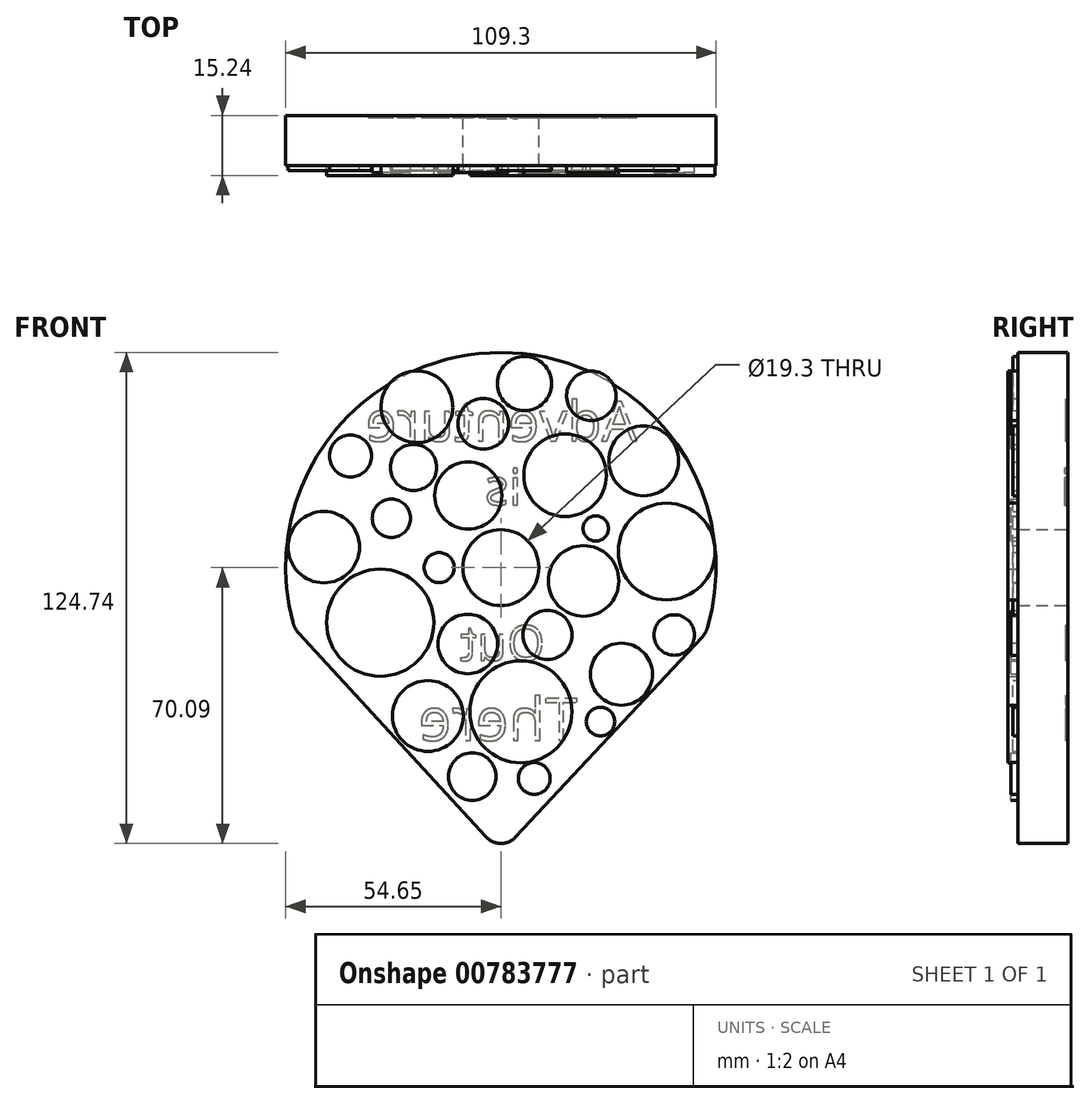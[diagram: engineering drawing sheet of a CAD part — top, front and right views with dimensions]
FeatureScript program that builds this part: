
annotation { "Feature Type Name" : "Feature", "Feature Type Description" : "" }
export const myFeature = defineFeature(function(context is Context, id is Id, definition is map)
    precondition{}
    {
        {
            var Q0;
            Q0=qCreatedBy(makeId("Front.planeOp"),FACE);
            var sketch = newSketch(context, id + "F0", { "sketchPlane" : qUnion([Q0])});
            skCircle(sketch, "E0", {"center": v(0, 0) * mm, "radius": 9.65 * mm});
            skArc(sketch, "E1", {"start": v(52.5, -15.18) * mm, "mid": v(0.62, 54.64) * mm, "end": v(-52.83, -13.99) * mm});
            skLineSegment(sketch, "E2", {"start": v(-51.36, -16.66) * mm, "end": v(-0.8, -71.62) * mm});
            skLineSegment(sketch, "E3", {"start": v(0.07, -72.4) * mm, "end": v(51.04, -17.75) * mm});
            skPoint(sketch, "E4.visualSharp", {"position": v(0, -72.49) * mm});
            skArc(sketch, "E4.filletArc", {"start": v(-0.8, -71.62) * mm, "mid": v(-0.38, -72.03) * mm, "end": v(0.07, -72.4) * mm});
            skPoint(sketch, "E5.visualSharp", {"position": v(-52.39, -15.54) * mm});
            skArc(sketch, "E5.filletArc", {"start": v(-52.83, -13.99) * mm, "mid": v(-52.26, -15.41) * mm, "end": v(-51.36, -16.66) * mm});
            skPoint(sketch, "E6.visualSharp", {"position": v(52.04, -16.68) * mm});
            skArc(sketch, "E6.filletArc", {"start": v(51.04, -17.75) * mm, "mid": v(51.92, -16.55) * mm, "end": v(52.5, -15.18) * mm});
            skSolve(sketch);
        }
        {
            var Q0;
            Q0=makeQuery(id+"F0.imprint","IMPRINT",FACE,{"disambiguationData":[TD([[makeQuery(id+"F0.imprint","IMPRINT",EDGE,{"derivedFrom":sQuery(id+"F0.wireOp",EDGE,"E0")}),-1.0]])]});
            extrude(context, id + "F1", {"entities" : qUnion([Q0]), "depth" : 12.7 * mm, "offsetDistance" : 25.4 * mm});
        }
        {
            var Q0;
            Q0=makeQuery(id+"F1.opExtrude","CAP_FACE",FACE,{"disambiguationData":[OSD([sQuery(id+"F0.wireOp",EDGE,"E0"),sQuery(id+"F0.wireOp",EDGE,"E1"),sQuery(id+"F0.wireOp",EDGE,"E2"),sQuery(id+"F0.wireOp",EDGE,"E3"),sQuery(id+"F0.wireOp",EDGE,"E4.filletArc"),sQuery(id+"F0.wireOp",EDGE,"E5.filletArc"),sQuery(id+"F0.wireOp",EDGE,"E6.filletArc")])],"isStart":true});
            var sketch = newSketch(context, id + "F2", { "sketchPlane" : qUnion([Q0])});
            skText(sketch, "E7", { "text": "Adventure", "fontName": "NotoSans-Regular.ttf"});
            const initialGuessF2  = {"E7": [-0.03457, 0.03213, 1, 0, 0.01013]};
            skSetInitialGuess(sketch, initialGuessF2);
            skSolve(sketch);
        }
        {
            var Q0;
            Q0 = qSketchRegion(id + "F2", true);
            extrude(context, id + "F3", {"entities" : qUnion([Q0]), "operationType" : NewBodyOperationType.REMOVE, "oppositeDirection" : true, "depth" : 0.5 * mm, "offsetDistance" : 25.4 * mm});
        }
        {
            var Q0;
            {var subQ0=sQuery(id+"F0.wireOp",EDGE,"E1");var subQ1=sQuery(id+"F0.wireOp",EDGE,"E3");var subQ2=sQuery(id+"F0.wireOp",EDGE,"E0");var subQ3=sQuery(id+"F0.wireOp",EDGE,"E4.filletArc");var subQ4=sQuery(id+"F0.wireOp",EDGE,"E5.filletArc");var subQ5=sQuery(id+"F0.wireOp",EDGE,"E6.filletArc");var subQ6=sQuery(id+"F0.wireOp",EDGE,"E2");Q0=makeQuery(id+"F3.boolean.opBoolean","SPLIT",FACE,{"disambiguationData":[TD([makeQuery(id+"F1.opExtrude","SWEPT_FACE",FACE,{"disambiguationData":[OSD([subQ2])]})])],"derivedFrom":makeQuery(id+"F1.opExtrude","CAP_FACE",FACE,{"disambiguationData":[OSD([subQ2,subQ0,subQ6,subQ1,subQ3,subQ4,subQ5])],"isStart":true})});}
            var sketch = newSketch(context, id + "F4", { "sketchPlane" : qUnion([Q0])});
            skText(sketch, "E8", { "text": "is", "fontName": "OpenSans-Regular.ttf"});
            const initialGuessF4  = {"E8": [-0.00527, 0.01596, 1, 0, 0.00921]};
            skSetInitialGuess(sketch, initialGuessF4);
            skSolve(sketch);
        }
        {
            var Q0;
            Q0 = qSketchRegion(id + "F4", true);
            extrude(context, id + "F5", {"entities" : qUnion([Q0]), "operationType" : NewBodyOperationType.REMOVE, "oppositeDirection" : true, "depth" : 0.76 * mm, "offsetDistance" : 25.4 * mm});
        }
        {
            var Q0;
            {var subQ0=sQuery(id+"F0.wireOp",EDGE,"E1");var subQ1=sQuery(id+"F0.wireOp",EDGE,"E3");var subQ2=sQuery(id+"F0.wireOp",EDGE,"E0");var subQ3=sQuery(id+"F0.wireOp",EDGE,"E4.filletArc");var subQ4=sQuery(id+"F0.wireOp",EDGE,"E5.filletArc");var subQ5=sQuery(id+"F0.wireOp",EDGE,"E6.filletArc");var subQ6=sQuery(id+"F0.wireOp",EDGE,"E2");Q0=makeQuery(id+"F3.boolean.opBoolean","SPLIT",FACE,{"disambiguationData":[TD([makeQuery(id+"F1.opExtrude","SWEPT_FACE",FACE,{"disambiguationData":[OSD([subQ2])]})])],"derivedFrom":makeQuery(id+"F1.opExtrude","CAP_FACE",FACE,{"disambiguationData":[OSD([subQ2,subQ0,subQ6,subQ1,subQ3,subQ4,subQ5])],"isStart":true})});}
            var sketch = newSketch(context, id + "F6", { "sketchPlane" : qUnion([Q0])});
            skText(sketch, "E9", { "text": "Out", "fontName": "OpenSans-Regular.ttf"});
            const initialGuessF6  = {"E9": [-0.0112, -0.0236, 1, 0, 0.00894]};
            skSetInitialGuess(sketch, initialGuessF6);
            skSolve(sketch);
        }
        {
            var Q0;
            Q0 = qSketchRegion(id + "F6", true);
            extrude(context, id + "F7", {"entities" : qUnion([Q0]), "operationType" : NewBodyOperationType.REMOVE, "oppositeDirection" : true, "depth" : 0.5 * mm, "offsetDistance" : 25.4 * mm});
        }
        {
            var Q0;
            {var subQ61=sQuery(id+"F0.wireOp",EDGE,"E6.filletArc");var subQ68=sQuery(id+"F0.wireOp",EDGE,"E5.filletArc");var subQ77=sQuery(id+"F0.wireOp",EDGE,"E0");var subQ78=makeQuery(id+"F1.opExtrude","SWEPT_FACE",FACE,{"disambiguationData":[OSD([subQ77])]});var subQ81=sQuery(id+"F0.wireOp",EDGE,"E4.filletArc");var subQ87=sQuery(id+"F0.wireOp",EDGE,"E3");var subQ91=sQuery(id+"F0.wireOp",EDGE,"E1");var subQ94=sQuery(id+"F0.wireOp",EDGE,"E2");Q0=makeQuery(id+"F7.boolean.opBoolean","SPLIT",FACE,{"disambiguationData":[TD([subQ78])],"derivedFrom":makeQuery(id+"F3.boolean.opBoolean","SPLIT",FACE,{"disambiguationData":[TD([subQ78])],"derivedFrom":makeQuery(id+"F1.opExtrude","CAP_FACE",FACE,{"disambiguationData":[OSD([subQ77,subQ91,subQ94,subQ87,subQ81,subQ68,subQ61])],"isStart":true})})});}
            var sketch = newSketch(context, id + "F8", { "sketchPlane" : qUnion([Q0])});
            skText(sketch, "E10", { "text": "There", "fontName": "OpenSans-Regular.ttf"});
            const initialGuessF8  = {"E10": [-0.01947, -0.0439, 1, 0, 0.01079]};
            skSetInitialGuess(sketch, initialGuessF8);
            skSolve(sketch);
        }
        {
            var Q0;
            Q0 = qSketchRegion(id + "F8", true);
            extrude(context, id + "F9", {"entities" : qUnion([Q0]), "operationType" : NewBodyOperationType.REMOVE, "oppositeDirection" : true, "depth" : 0.5 * mm, "offsetDistance" : 25.4 * mm});
        }
        {
            var Q0;
            Q0=makeQuery(id+"F1.opExtrude","CAP_FACE",FACE,{"disambiguationData":[OSD([sQuery(id+"F0.wireOp",EDGE,"E0"),sQuery(id+"F0.wireOp",EDGE,"E1"),sQuery(id+"F0.wireOp",EDGE,"E2"),sQuery(id+"F0.wireOp",EDGE,"E3"),sQuery(id+"F0.wireOp",EDGE,"E4.filletArc"),sQuery(id+"F0.wireOp",EDGE,"E5.filletArc"),sQuery(id+"F0.wireOp",EDGE,"E6.filletArc")])],"isStart":false});
            var sketch = newSketch(context, id + "F10", { "sketchPlane" : qUnion([Q0])});
            skCircle(sketch, "E11", {"center": v(-21.32, 40.87) * mm, "radius": 9.11 * mm});
            skCircle(sketch, "E12", {"center": v(16.3, 23.46) * mm, "radius": 10.48 * mm});
            skCircle(sketch, "E13", {"center": v(-30.64, -13.99) * mm, "radius": 13.62 * mm});
            skCircle(sketch, "E14", {"center": v(30.63, -27.08) * mm, "radius": 7.88 * mm});
            skCircle(sketch, "E15", {"center": v(5.07, -36.63) * mm, "radius": 12.96 * mm});
            skCircle(sketch, "E16", {"center": v(42.14, 4.09) * mm, "radius": 12.3 * mm});
            skSolve(sketch);
        }
        {
            var Q0;
            Q0=makeQuery(id+"F10.imprint","IMPRINT",FACE,{"disambiguationData":[TD([[makeQuery(id+"F10.imprint","IMPRINT",EDGE,{"derivedFrom":sQuery(id+"F10.wireOp",EDGE,"E11")}),1.0]])]});
            var Q1;
            Q1=makeQuery(id+"F10.imprint","IMPRINT",FACE,{"disambiguationData":[TD([[makeQuery(id+"F10.imprint","IMPRINT",EDGE,{"derivedFrom":sQuery(id+"F10.wireOp",EDGE,"E12")}),1.0]])]});
            var Q2;
            Q2=makeQuery(id+"F10.imprint","IMPRINT",FACE,{"disambiguationData":[TD([[makeQuery(id+"F10.imprint","IMPRINT",EDGE,{"derivedFrom":sQuery(id+"F10.wireOp",EDGE,"E16")}),1.0]])]});
            var Q3;
            Q3=makeQuery(id+"F10.imprint","IMPRINT",FACE,{"disambiguationData":[TD([[makeQuery(id+"F10.imprint","IMPRINT",EDGE,{"derivedFrom":sQuery(id+"F10.wireOp",EDGE,"E14")}),1.0]])]});
            var Q4;
            Q4=makeQuery(id+"F10.imprint","IMPRINT",FACE,{"disambiguationData":[TD([[makeQuery(id+"F10.imprint","IMPRINT",EDGE,{"derivedFrom":sQuery(id+"F10.wireOp",EDGE,"E15")}),1.0]])]});
            var Q5;
            Q5=makeQuery(id+"F10.imprint","IMPRINT",FACE,{"disambiguationData":[TD([[makeQuery(id+"F10.imprint","IMPRINT",EDGE,{"derivedFrom":sQuery(id+"F10.wireOp",EDGE,"E13")}),1.0]])]});
            extrude(context, id + "F11", {"entities" : qUnion([Q0, Q1, Q2, Q3, Q4, Q5]), "operationType" : NewBodyOperationType.ADD, "depth" : 2.54 * mm, "offsetDistance" : 25.4 * mm});
        }
        {
            var Q0;
            Q0=makeQuery(id+"F1.opExtrude","CAP_FACE",FACE,{"disambiguationData":[OSD([sQuery(id+"F0.wireOp",EDGE,"E0"),sQuery(id+"F0.wireOp",EDGE,"E1"),sQuery(id+"F0.wireOp",EDGE,"E2"),sQuery(id+"F0.wireOp",EDGE,"E3"),sQuery(id+"F0.wireOp",EDGE,"E4.filletArc"),sQuery(id+"F0.wireOp",EDGE,"E5.filletArc"),sQuery(id+"F0.wireOp",EDGE,"E6.filletArc")])],"isStart":false});
            var sketch = newSketch(context, id + "F12", { "sketchPlane" : qUnion([Q0])});
            skCircle(sketch, "E17", {"center": v(-4.45, 36.53) * mm, "radius": 6.45 * mm});
            skCircle(sketch, "E18", {"center": v(22.97, 43.64) * mm, "radius": 6.28 * mm});
            skCircle(sketch, "E19", {"center": v(-7.27, -53.07) * mm, "radius": 6.05 * mm});
            skCircle(sketch, "E20", {"center": v(-8.41, -19.4) * mm, "radius": 7.55 * mm});
            skCircle(sketch, "E21", {"center": v(-27.8, 12.55) * mm, "radius": 4.88 * mm});
            skCircle(sketch, "E22", {"center": v(11.85, -17.12) * mm, "radius": 6.23 * mm});
            skCircle(sketch, "E23", {"center": v(44.07, -17.12) * mm, "radius": 5.14 * mm});
            skCircle(sketch, "E24", {"center": v(8.47, -53.57) * mm, "radius": 4.05 * mm});
            skCircle(sketch, "E25", {"center": v(24.1, 9.95) * mm, "radius": 3.22 * mm});
            skSolve(sketch);
        }
        {
            var Q0;
            Q0=makeQuery(id+"F12.imprint","IMPRINT",FACE,{"disambiguationData":[TD([[makeQuery(id+"F12.imprint","IMPRINT",EDGE,{"derivedFrom":sQuery(id+"F12.wireOp",EDGE,"E17")}),1.0]])]});
            var Q1;
            Q1=makeQuery(id+"F12.imprint","IMPRINT",FACE,{"disambiguationData":[TD([[makeQuery(id+"F12.imprint","IMPRINT",EDGE,{"derivedFrom":sQuery(id+"F12.wireOp",EDGE,"E21")}),1.0]])]});
            var Q2;
            Q2=makeQuery(id+"F12.imprint","IMPRINT",FACE,{"disambiguationData":[TD([[makeQuery(id+"F12.imprint","IMPRINT",EDGE,{"derivedFrom":sQuery(id+"F12.wireOp",EDGE,"E18")}),1.0]])]});
            var Q3;
            Q3=makeQuery(id+"F12.imprint","IMPRINT",FACE,{"disambiguationData":[TD([[makeQuery(id+"F12.imprint","IMPRINT",EDGE,{"derivedFrom":sQuery(id+"F12.wireOp",EDGE,"E25")}),1.0]])]});
            var Q4;
            Q4=makeQuery(id+"F12.imprint","IMPRINT",FACE,{"disambiguationData":[TD([[makeQuery(id+"F12.imprint","IMPRINT",EDGE,{"derivedFrom":sQuery(id+"F12.wireOp",EDGE,"E22")}),1.0]])]});
            var Q5;
            Q5=makeQuery(id+"F12.imprint","IMPRINT",FACE,{"disambiguationData":[TD([[makeQuery(id+"F12.imprint","IMPRINT",EDGE,{"derivedFrom":sQuery(id+"F12.wireOp",EDGE,"E20")}),1.0]])]});
            var Q6;
            Q6=makeQuery(id+"F12.imprint","IMPRINT",FACE,{"disambiguationData":[TD([[makeQuery(id+"F12.imprint","IMPRINT",EDGE,{"derivedFrom":sQuery(id+"F12.wireOp",EDGE,"E19")}),1.0]])]});
            var Q7;
            Q7=makeQuery(id+"F12.imprint","IMPRINT",FACE,{"disambiguationData":[TD([[makeQuery(id+"F12.imprint","IMPRINT",EDGE,{"derivedFrom":sQuery(id+"F12.wireOp",EDGE,"E24")}),1.0]])]});
            var Q8;
            Q8=makeQuery(id+"F12.imprint","IMPRINT",FACE,{"disambiguationData":[TD([[makeQuery(id+"F12.imprint","IMPRINT",EDGE,{"derivedFrom":sQuery(id+"F12.wireOp",EDGE,"E23")}),1.0]])]});
            extrude(context, id + "F13", {"entities" : qUnion([Q0, Q1, Q2, Q3, Q4, Q5, Q6, Q7, Q8]), "operationType" : NewBodyOperationType.ADD, "depth" : 1.78 * mm, "offsetDistance" : 25.4 * mm});
        }
        {
            var Q0;
            Q0=makeQuery(id+"F1.opExtrude","CAP_FACE",FACE,{"disambiguationData":[OSD([sQuery(id+"F0.wireOp",EDGE,"E0"),sQuery(id+"F0.wireOp",EDGE,"E1"),sQuery(id+"F0.wireOp",EDGE,"E2"),sQuery(id+"F0.wireOp",EDGE,"E3"),sQuery(id+"F0.wireOp",EDGE,"E4.filletArc"),sQuery(id+"F0.wireOp",EDGE,"E5.filletArc"),sQuery(id+"F0.wireOp",EDGE,"E6.filletArc")])],"isStart":false});
            var sketch = newSketch(context, id + "F14", { "sketchPlane" : qUnion([Q0])});
            skCircle(sketch, "E26", {"center": v(-38.2, 28.36) * mm, "radius": 5.34 * mm});
            skCircle(sketch, "E27", {"center": v(-22.18, 25.45) * mm, "radius": 5.87 * mm});
            skCircle(sketch, "E28", {"center": v(-8.29, 18.3) * mm, "radius": 8.53 * mm});
            skCircle(sketch, "E29", {"center": v(-44.98, 5.2) * mm, "radius": 9.07 * mm});
            skCircle(sketch, "E30", {"center": v(36.27, 27.12) * mm, "radius": 8.87 * mm});
            skCircle(sketch, "E31", {"center": v(6, 46.77) * mm, "radius": 6.9 * mm});
            skCircle(sketch, "E32", {"center": v(-18.53, -37.7) * mm, "radius": 9 * mm});
            skCircle(sketch, "E33", {"center": v(21.02, -3.38) * mm, "radius": 8.97 * mm});
            skCircle(sketch, "E34", {"center": v(-15.67, 0) * mm, "radius": 3.81 * mm});
            skCircle(sketch, "E35", {"center": v(25.31, -39.12) * mm, "radius": 3.63 * mm});
            skSolve(sketch);
        }
        {
            var Q0;
            Q0=makeQuery(id+"F14.imprint","IMPRINT",FACE,{"disambiguationData":[TD([[makeQuery(id+"F14.imprint","IMPRINT",EDGE,{"derivedFrom":sQuery(id+"F14.wireOp",EDGE,"E26")}),1.0]])]});
            var Q1;
            Q1=makeQuery(id+"F14.imprint","IMPRINT",FACE,{"disambiguationData":[TD([[makeQuery(id+"F14.imprint","IMPRINT",EDGE,{"derivedFrom":sQuery(id+"F14.wireOp",EDGE,"E27")}),1.0]])]});
            var Q2;
            Q2=makeQuery(id+"F14.imprint","IMPRINT",FACE,{"disambiguationData":[TD([[makeQuery(id+"F14.imprint","IMPRINT",EDGE,{"derivedFrom":sQuery(id+"F14.wireOp",EDGE,"E28")}),1.0]])]});
            var Q3;
            Q3=makeQuery(id+"F14.imprint","IMPRINT",FACE,{"disambiguationData":[TD([[makeQuery(id+"F14.imprint","IMPRINT",EDGE,{"derivedFrom":sQuery(id+"F14.wireOp",EDGE,"E29")}),1.0]])]});
            var Q4;
            Q4=makeQuery(id+"F14.imprint","IMPRINT",FACE,{"disambiguationData":[TD([[makeQuery(id+"F14.imprint","IMPRINT",EDGE,{"derivedFrom":sQuery(id+"F14.wireOp",EDGE,"E34")}),1.0]])]});
            var Q5;
            Q5=makeQuery(id+"F14.imprint","IMPRINT",FACE,{"disambiguationData":[TD([[makeQuery(id+"F14.imprint","IMPRINT",EDGE,{"derivedFrom":sQuery(id+"F14.wireOp",EDGE,"E32")}),1.0]])]});
            var Q6;
            Q6=makeQuery(id+"F14.imprint","IMPRINT",FACE,{"disambiguationData":[TD([[makeQuery(id+"F14.imprint","IMPRINT",EDGE,{"derivedFrom":sQuery(id+"F14.wireOp",EDGE,"E35")}),1.0]])]});
            var Q7;
            Q7=makeQuery(id+"F14.imprint","IMPRINT",FACE,{"disambiguationData":[TD([[makeQuery(id+"F14.imprint","IMPRINT",EDGE,{"derivedFrom":sQuery(id+"F14.wireOp",EDGE,"E33")}),1.0]])]});
            var Q8;
            Q8=makeQuery(id+"F14.imprint","IMPRINT",FACE,{"disambiguationData":[TD([[makeQuery(id+"F14.imprint","IMPRINT",EDGE,{"derivedFrom":sQuery(id+"F14.wireOp",EDGE,"E30")}),1.0]])]});
            var Q9;
            Q9=makeQuery(id+"F14.imprint","IMPRINT",FACE,{"disambiguationData":[TD([[makeQuery(id+"F14.imprint","IMPRINT",EDGE,{"derivedFrom":sQuery(id+"F14.wireOp",EDGE,"E31")}),1.0]])]});
            extrude(context, id + "F15", {"entities" : qUnion([Q0, Q1, Q2, Q3, Q4, Q5, Q6, Q7, Q8, Q9]), "operationType" : NewBodyOperationType.ADD, "depth" : 1.27 * mm, "offsetDistance" : 25.4 * mm});
        }
        {
            var Q0;
            Q0=makeQuery(id+"F1.opExtrude","SWEPT_EDGE",EDGE,{"disambiguationData":[OSD([sQuery(id+"F0.wireOp",EDGE,"E2"),sQuery(id+"F0.wireOp",EDGE,"E4.filletArc")])]});
            var Q1;
            Q1=makeQuery(id+"F1.opExtrude","SWEPT_EDGE",EDGE,{"disambiguationData":[OSD([sQuery(id+"F0.wireOp",EDGE,"E3"),sQuery(id+"F0.wireOp",EDGE,"E4.filletArc")])]});
            fillet(context, id + "F16", {"entities" : qUnion([Q0, Q1]), "radius" : 5.08 * mm, "tangentPropagation" : true, "allowEdgeOverflow" : false});
        }
    });
